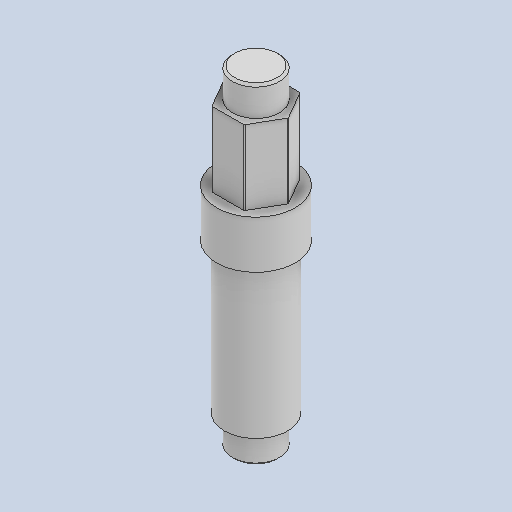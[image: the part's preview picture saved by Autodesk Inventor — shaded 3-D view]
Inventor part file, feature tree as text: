
AUTODESK INVENTOR PART (.ipt)
format: ipt  version: 2022.3 (Build 263350000, 350)  size: 108,032 bytes
history: native  units: in
note: dims shown in document units (in); Inventor stores cm internally (conversion verified against a paired STEP export)
features: chamfer x1
ambient origin geometry x8: Origin, YZ Plane, XZ Plane, XY Plane, X Axis, Y Axis, Z Axis, Center Point
bodies: Solid1 (feature_tree)
feature tree (1):
  chamfer  "Chamfer1"  [1 undecoded]
note: 1 required parameter value undecoded (feature->parameter linkage not recoverable at this tier; creation-order binding heuristic only, values carry confidence <= 0.55)
